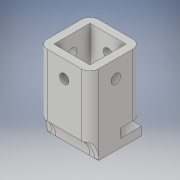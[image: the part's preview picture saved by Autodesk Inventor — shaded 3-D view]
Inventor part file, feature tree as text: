
AUTODESK INVENTOR PART (.ipt)
format: ipt  version: 2019.4 (Build 234330000, 330)  size: 224,256 bytes
history: native  units: mm
features: extrude x8, sketch x8, fillet x2
ambient origin geometry x8: Origin, YZ Plane, XZ Plane, XY Plane, X Axis, Y Axis, Z Axis, Center Point
bodies: Solid1 (feature_tree)
feature tree (18):
  extrude  "Extrusion1"  Depth=30.0mm
  extrude  "Extrusion2"  Depth=4.5mm
  extrude  "Extrusion3"  Depth=21.0mm
  fillet  "Fillet2"  Radius=21.0mm
  extrude  "Extrusion4"  Depth=15.0mm
  extrude  "Extrusion5"  Depth=5.0mm TaperAngle=0.0deg
  fillet  "Fillet3"  Radius=5.0mm
  extrude  "Extrusion6"  Depth=10.0mm
  extrude  "Extrusion7"  TaperAngle=60.0deg  [1 undecoded]
  extrude  "Extrusion8"  Depth=10.0mm
  sketch  "Sketch1"  dims[d0=30.0mm d1=30.0mm]
  sketch  "Sketch2"  dims[d2=36.35mm d3=0.0mm d4=4.5mm]
  sketch  "Sketch3"  dims[d5=4.5mm d6=21.0mm d7=21.0mm]
  sketch  "Sketch4"  dims[d8=30.0mm d9=0.0mm d10=15.0mm]
  sketch  "Sketch5"  dims[d11=4.0mm d12=5.0mm d13=0.0mm d15=5.0mm]
  sketch  "Sketch6"  dims[d16=10.0mm d17=6.0mm]
  sketch  "Sketch7"  dims[d18=90.0deg d19=60.0deg]
  sketch  "Sketch8"  dims[d20=5.0mm d21=0.0mm d22=30.0mm d23=25.0mm d24=5.0mm d25=0.0mm d26=13.0mm d27=10.0mm d28=90.0deg d29=5.5mm d30=30.0mm d31=0.0mm d32=10.0mm d33=90.0deg d34=5.5mm d35=30.0mm d36=0.0mm d37=4.0mm d38=5.0mm d39=0.0mm]
note: 1 required parameter value undecoded (feature->parameter linkage not recoverable at this tier; creation-order binding heuristic only, values carry confidence <= 0.55)
